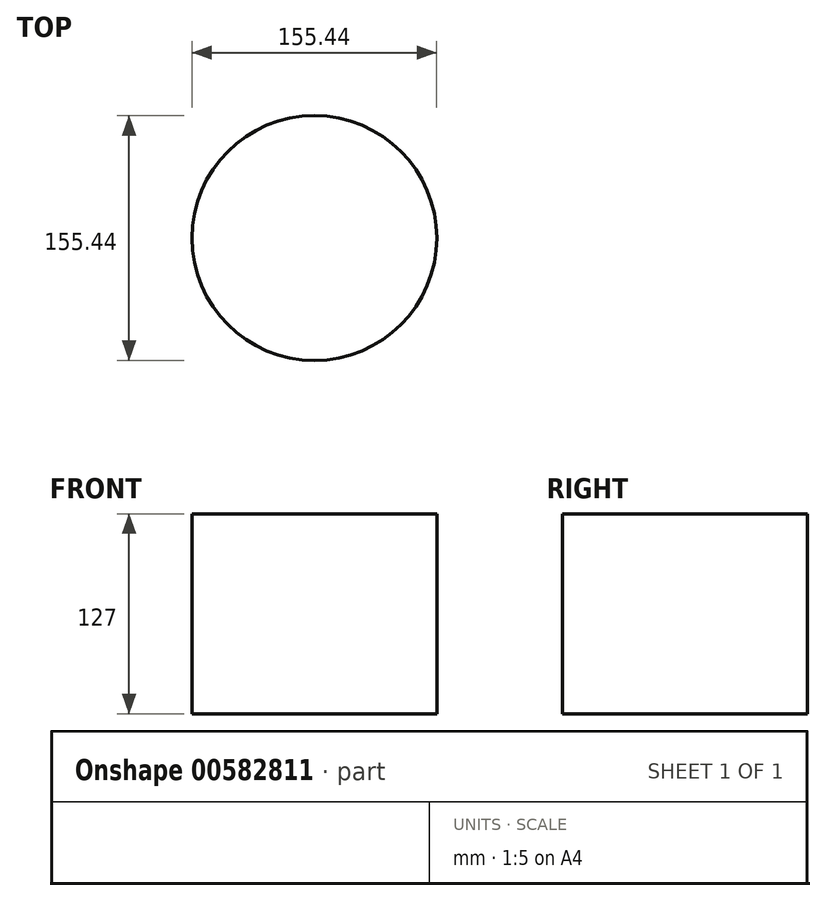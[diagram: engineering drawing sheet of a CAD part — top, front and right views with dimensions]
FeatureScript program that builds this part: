
annotation { "Feature Type Name" : "Feature", "Feature Type Description" : "" }
export const myFeature = defineFeature(function(context is Context, id is Id, definition is map)
    precondition{}
    {
        {
            var Q0;
            Q0=qCreatedBy(makeId("Top.planeOp"),FACE);
            var sketch = newSketch(context, id + "F0", { "sketchPlane" : qUnion([Q0])});
            skCircle(sketch, "E0", {"center": v(0, 0) * mm, "radius": 77.72 * mm});
            skSolve(sketch);
        }
        {
            var Q0;
            Q0=makeQuery(id+"F0.imprint","IMPRINT",FACE,{"disambiguationData":[TD([[makeQuery(id+"F0.imprint","IMPRINT",EDGE,{"derivedFrom":sQuery(id+"F0.wireOp",EDGE,"E0")}),1.0]])]});
            extrude(context, id + "F1", {"entities" : qUnion([Q0]), "depth" : 127 * mm, "offsetDistance" : 25.4 * mm});
        }
    });
